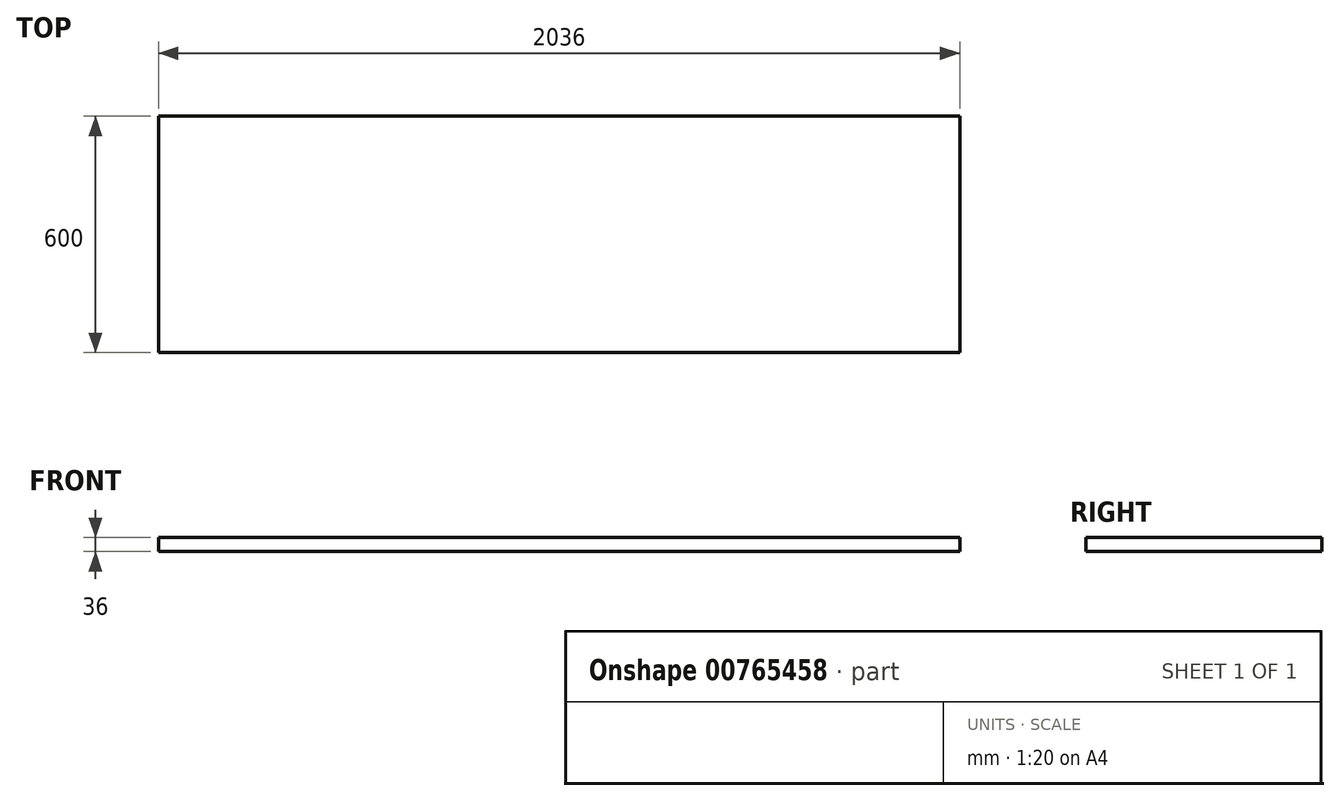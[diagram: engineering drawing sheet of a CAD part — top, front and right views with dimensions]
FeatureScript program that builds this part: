
annotation { "Feature Type Name" : "Feature", "Feature Type Description" : "" }
export const myFeature = defineFeature(function(context is Context, id is Id, definition is map)
    precondition{}
    {
        {
            var Q0;
            Q0=qCreatedBy(makeId("Top.planeOp"),FACE);
            var sketch = newSketch(context, id + "F0", { "sketchPlane" : qUnion([Q0])});
            skLineSegment(sketch, "E0.bottom", {"start": v(-1018, -300) * mm, "end": v(1018, -300) * mm});
            skLineSegment(sketch, "E0.top", {"start": v(-1018, 300) * mm, "end": v(1018, 300) * mm});
            skLineSegment(sketch, "E0.left", {"start": v(-1018, -300) * mm, "end": v(-1018, 300) * mm});
            skLineSegment(sketch, "E0.right", {"start": v(1018, -300) * mm, "end": v(1018, 300) * mm});
            skPoint(sketch, "E0.middle", {"position": v(0, 0) * mm});
            skSolve(sketch);
        }
        {
            var Q0;
            Q0 = qSketchRegion(id + "F0", true);
            extrude(context, id + "F1", {"entities" : qUnion([Q0]), "oppositeDirection" : true, "depth" : 36 * mm, "offsetDistance" : 25 * mm});
        }
    });
